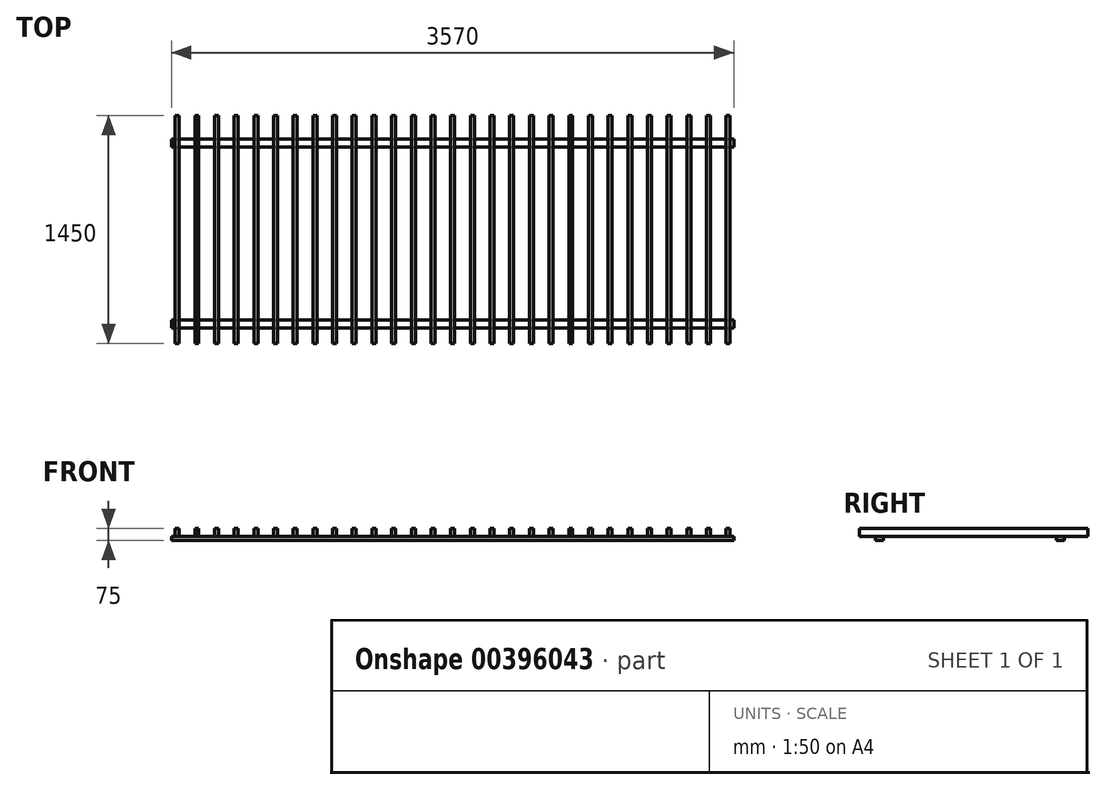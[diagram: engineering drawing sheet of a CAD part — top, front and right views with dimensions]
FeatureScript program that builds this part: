
annotation { "Feature Type Name" : "Feature", "Feature Type Description" : "" }
export const myFeature = defineFeature(function(context is Context, id is Id, definition is map)
    precondition{}
    {
        {
            var Q0;
            Q0=qCreatedBy(makeId("Top.planeOp"),FACE);
            var sketch = newSketch(context, id + "F0", { "sketchPlane" : qUnion([Q0])});
            skLineSegment(sketch, "E0.bottom", {"start": v(0, 0) * mm, "end": v(3570, 0) * mm, "construction": true});
            skLineSegment(sketch, "E0.top", {"start": v(0, 1500) * mm, "end": v(3570, 1500) * mm, "construction": true});
            skLineSegment(sketch, "E0.left", {"start": v(0, 0) * mm, "end": v(0, 1500) * mm, "construction": true});
            skLineSegment(sketch, "E0.right", {"start": v(3570, 0) * mm, "end": v(3570, 1500) * mm, "construction": true});
            skLineSegment(sketch, "E1", {"start": v(0, 750) * mm, "end": v(3570, 750) * mm, "construction": true});
            skLineSegment(sketch, "E2.bottom", {"start": v(22.5, 1500) * mm, "end": v(47.5, 1500) * mm});
            skLineSegment(sketch, "E2.top", {"start": v(22.5, 50) * mm, "end": v(47.5, 50) * mm});
            skLineSegment(sketch, "E2.left", {"start": v(22.5, 1500) * mm, "end": v(22.5, 50) * mm});
            skLineSegment(sketch, "E2.right", {"start": v(47.5, 1500) * mm, "end": v(47.5, 50) * mm});
            skLineSegment(sketch, "E3.1.0.0", {"start": v(147.5, 1500) * mm, "end": v(147.5, 50) * mm});
            skLineSegment(sketch, "E3.1.0.1", {"start": v(172.5, 1500) * mm, "end": v(172.5, 50) * mm});
            skLineSegment(sketch, "E3.1.0.2", {"start": v(147.5, 1500) * mm, "end": v(172.5, 1500) * mm});
            skLineSegment(sketch, "E3.1.0.3", {"start": v(147.5, 50) * mm, "end": v(172.5, 50) * mm});
            skLineSegment(sketch, "E3.2.0.0", {"start": v(272.5, 1500) * mm, "end": v(272.5, 50) * mm});
            skLineSegment(sketch, "E3.2.0.1", {"start": v(297.5, 1500) * mm, "end": v(297.5, 50) * mm});
            skLineSegment(sketch, "E3.2.0.2", {"start": v(272.5, 1500) * mm, "end": v(297.5, 1500) * mm});
            skLineSegment(sketch, "E3.2.0.3", {"start": v(272.5, 50) * mm, "end": v(297.5, 50) * mm});
            skLineSegment(sketch, "E3.3.0.0", {"start": v(397.5, 1500) * mm, "end": v(397.5, 50) * mm});
            skLineSegment(sketch, "E3.3.0.1", {"start": v(422.5, 1500) * mm, "end": v(422.5, 50) * mm});
            skLineSegment(sketch, "E3.3.0.2", {"start": v(397.5, 1500) * mm, "end": v(422.5, 1500) * mm});
            skLineSegment(sketch, "E3.3.0.3", {"start": v(397.5, 50) * mm, "end": v(422.5, 50) * mm});
            skLineSegment(sketch, "E3.4.0.0", {"start": v(522.5, 1500) * mm, "end": v(522.5, 50) * mm});
            skLineSegment(sketch, "E3.4.0.1", {"start": v(547.5, 1500) * mm, "end": v(547.5, 50) * mm});
            skLineSegment(sketch, "E3.4.0.2", {"start": v(522.5, 1500) * mm, "end": v(547.5, 1500) * mm});
            skLineSegment(sketch, "E3.4.0.3", {"start": v(522.5, 50) * mm, "end": v(547.5, 50) * mm});
            skLineSegment(sketch, "E3.5.0.0", {"start": v(647.5, 1500) * mm, "end": v(647.5, 50) * mm});
            skLineSegment(sketch, "E3.5.0.1", {"start": v(672.5, 1500) * mm, "end": v(672.5, 50) * mm});
            skLineSegment(sketch, "E3.5.0.2", {"start": v(647.5, 1500) * mm, "end": v(672.5, 1500) * mm});
            skLineSegment(sketch, "E3.5.0.3", {"start": v(647.5, 50) * mm, "end": v(672.5, 50) * mm});
            skLineSegment(sketch, "E3.6.0.0", {"start": v(772.5, 1500) * mm, "end": v(772.5, 50) * mm});
            skLineSegment(sketch, "E3.6.0.1", {"start": v(797.5, 1500) * mm, "end": v(797.5, 50) * mm});
            skLineSegment(sketch, "E3.6.0.2", {"start": v(772.5, 1500) * mm, "end": v(797.5, 1500) * mm});
            skLineSegment(sketch, "E3.6.0.3", {"start": v(772.5, 50) * mm, "end": v(797.5, 50) * mm});
            skLineSegment(sketch, "E3.7.0.0", {"start": v(897.5, 1500) * mm, "end": v(897.5, 50) * mm});
            skLineSegment(sketch, "E3.7.0.1", {"start": v(922.5, 1500) * mm, "end": v(922.5, 50) * mm});
            skLineSegment(sketch, "E3.7.0.2", {"start": v(897.5, 1500) * mm, "end": v(922.5, 1500) * mm});
            skLineSegment(sketch, "E3.7.0.3", {"start": v(897.5, 50) * mm, "end": v(922.5, 50) * mm});
            skLineSegment(sketch, "E3.8.0.0", {"start": v(1022.5, 1500) * mm, "end": v(1022.5, 50) * mm});
            skLineSegment(sketch, "E3.8.0.1", {"start": v(1047.5, 1500) * mm, "end": v(1047.5, 50) * mm});
            skLineSegment(sketch, "E3.8.0.2", {"start": v(1022.5, 1500) * mm, "end": v(1047.5, 1500) * mm});
            skLineSegment(sketch, "E3.8.0.3", {"start": v(1022.5, 50) * mm, "end": v(1047.5, 50) * mm});
            skLineSegment(sketch, "E3.9.0.0", {"start": v(1147.5, 1500) * mm, "end": v(1147.5, 50) * mm});
            skLineSegment(sketch, "E3.9.0.1", {"start": v(1172.5, 1500) * mm, "end": v(1172.5, 50) * mm});
            skLineSegment(sketch, "E3.9.0.2", {"start": v(1147.5, 1500) * mm, "end": v(1172.5, 1500) * mm});
            skLineSegment(sketch, "E3.9.0.3", {"start": v(1147.5, 50) * mm, "end": v(1172.5, 50) * mm});
            skLineSegment(sketch, "E3.10.0.0", {"start": v(1272.5, 1500) * mm, "end": v(1272.5, 50) * mm});
            skLineSegment(sketch, "E3.10.0.1", {"start": v(1297.5, 1500) * mm, "end": v(1297.5, 50) * mm});
            skLineSegment(sketch, "E3.10.0.2", {"start": v(1272.5, 1500) * mm, "end": v(1297.5, 1500) * mm});
            skLineSegment(sketch, "E3.10.0.3", {"start": v(1272.5, 50) * mm, "end": v(1297.5, 50) * mm});
            skLineSegment(sketch, "E3.11.0.0", {"start": v(1397.5, 1500) * mm, "end": v(1397.5, 50) * mm});
            skLineSegment(sketch, "E3.11.0.1", {"start": v(1422.5, 1500) * mm, "end": v(1422.5, 50) * mm});
            skLineSegment(sketch, "E3.11.0.2", {"start": v(1397.5, 1500) * mm, "end": v(1422.5, 1500) * mm});
            skLineSegment(sketch, "E3.11.0.3", {"start": v(1397.5, 50) * mm, "end": v(1422.5, 50) * mm});
            skLineSegment(sketch, "E3.12.0.0", {"start": v(1522.5, 1500) * mm, "end": v(1522.5, 50) * mm});
            skLineSegment(sketch, "E3.12.0.1", {"start": v(1547.5, 1500) * mm, "end": v(1547.5, 50) * mm});
            skLineSegment(sketch, "E3.12.0.2", {"start": v(1522.5, 1500) * mm, "end": v(1547.5, 1500) * mm});
            skLineSegment(sketch, "E3.12.0.3", {"start": v(1522.5, 50) * mm, "end": v(1547.5, 50) * mm});
            skLineSegment(sketch, "E3.13.0.0", {"start": v(1647.5, 1500) * mm, "end": v(1647.5, 50) * mm});
            skLineSegment(sketch, "E3.13.0.1", {"start": v(1672.5, 1500) * mm, "end": v(1672.5, 50) * mm});
            skLineSegment(sketch, "E3.13.0.2", {"start": v(1647.5, 1500) * mm, "end": v(1672.5, 1500) * mm});
            skLineSegment(sketch, "E3.13.0.3", {"start": v(1647.5, 50) * mm, "end": v(1672.5, 50) * mm});
            skLineSegment(sketch, "E3.14.0.0", {"start": v(1772.5, 1500) * mm, "end": v(1772.5, 50) * mm});
            skLineSegment(sketch, "E3.14.0.1", {"start": v(1797.5, 1500) * mm, "end": v(1797.5, 50) * mm});
            skLineSegment(sketch, "E3.14.0.2", {"start": v(1772.5, 1500) * mm, "end": v(1797.5, 1500) * mm});
            skLineSegment(sketch, "E3.14.0.3", {"start": v(1772.5, 50) * mm, "end": v(1797.5, 50) * mm});
            skLineSegment(sketch, "E3.direction1", {"start": v(22.5, 50) * mm, "end": v(147.5, 50) * mm, "construction": true});
            skLineSegment(sketch, "E4.0.15.0", {"start": v(1897.5, 1500) * mm, "end": v(1897.5, 50) * mm});
            skLineSegment(sketch, "E4.3.15.0", {"start": v(1922.5, 1500) * mm, "end": v(1922.5, 50) * mm});
            skLineSegment(sketch, "E4.6.15.0", {"start": v(1897.5, 1500) * mm, "end": v(1922.5, 1500) * mm});
            skLineSegment(sketch, "E4.9.15.0", {"start": v(1897.5, 50) * mm, "end": v(1922.5, 50) * mm});
            skLineSegment(sketch, "E5.0.16.0", {"start": v(2022.5, 1500) * mm, "end": v(2022.5, 50) * mm});
            skLineSegment(sketch, "E5.3.16.0", {"start": v(2047.5, 1500) * mm, "end": v(2047.5, 50) * mm});
            skLineSegment(sketch, "E5.6.16.0", {"start": v(2022.5, 1500) * mm, "end": v(2047.5, 1500) * mm});
            skLineSegment(sketch, "E5.9.16.0", {"start": v(2022.5, 50) * mm, "end": v(2047.5, 50) * mm});
            skLineSegment(sketch, "E5.0.17.0", {"start": v(2147.5, 1500) * mm, "end": v(2147.5, 50) * mm});
            skLineSegment(sketch, "E5.3.17.0", {"start": v(2172.5, 1500) * mm, "end": v(2172.5, 50) * mm});
            skLineSegment(sketch, "E5.6.17.0", {"start": v(2147.5, 1500) * mm, "end": v(2172.5, 1500) * mm});
            skLineSegment(sketch, "E5.9.17.0", {"start": v(2147.5, 50) * mm, "end": v(2172.5, 50) * mm});
            skLineSegment(sketch, "E5.0.18.0", {"start": v(2272.5, 1500) * mm, "end": v(2272.5, 50) * mm});
            skLineSegment(sketch, "E5.3.18.0", {"start": v(2297.5, 1500) * mm, "end": v(2297.5, 50) * mm});
            skLineSegment(sketch, "E5.6.18.0", {"start": v(2272.5, 1500) * mm, "end": v(2297.5, 1500) * mm});
            skLineSegment(sketch, "E5.9.18.0", {"start": v(2272.5, 50) * mm, "end": v(2297.5, 50) * mm});
            skLineSegment(sketch, "E5.0.19.0", {"start": v(2397.5, 1500) * mm, "end": v(2397.5, 50) * mm});
            skLineSegment(sketch, "E5.3.19.0", {"start": v(2422.5, 1500) * mm, "end": v(2422.5, 50) * mm});
            skLineSegment(sketch, "E5.6.19.0", {"start": v(2397.5, 1500) * mm, "end": v(2422.5, 1500) * mm});
            skLineSegment(sketch, "E5.9.19.0", {"start": v(2397.5, 50) * mm, "end": v(2422.5, 50) * mm});
            skLineSegment(sketch, "E5.0.20.0", {"start": v(2522.5, 1500) * mm, "end": v(2522.5, 50) * mm});
            skLineSegment(sketch, "E5.3.20.0", {"start": v(2547.5, 1500) * mm, "end": v(2547.5, 50) * mm});
            skLineSegment(sketch, "E5.6.20.0", {"start": v(2522.5, 1500) * mm, "end": v(2547.5, 1500) * mm});
            skLineSegment(sketch, "E5.9.20.0", {"start": v(2522.5, 50) * mm, "end": v(2547.5, 50) * mm});
            skLineSegment(sketch, "E5.0.21.0", {"start": v(2647.5, 1500) * mm, "end": v(2647.5, 50) * mm});
            skLineSegment(sketch, "E5.3.21.0", {"start": v(2672.5, 1500) * mm, "end": v(2672.5, 50) * mm});
            skLineSegment(sketch, "E5.6.21.0", {"start": v(2647.5, 1500) * mm, "end": v(2672.5, 1500) * mm});
            skLineSegment(sketch, "E5.9.21.0", {"start": v(2647.5, 50) * mm, "end": v(2672.5, 50) * mm});
            skLineSegment(sketch, "E5.0.22.0", {"start": v(2772.5, 1500) * mm, "end": v(2772.5, 50) * mm});
            skLineSegment(sketch, "E5.3.22.0", {"start": v(2797.5, 1500) * mm, "end": v(2797.5, 50) * mm});
            skLineSegment(sketch, "E5.6.22.0", {"start": v(2772.5, 1500) * mm, "end": v(2797.5, 1500) * mm});
            skLineSegment(sketch, "E5.9.22.0", {"start": v(2772.5, 50) * mm, "end": v(2797.5, 50) * mm});
            skLineSegment(sketch, "E6.0.23.0", {"start": v(2897.5, 1500) * mm, "end": v(2897.5, 50) * mm});
            skLineSegment(sketch, "E6.3.23.0", {"start": v(2922.5, 1500) * mm, "end": v(2922.5, 50) * mm});
            skLineSegment(sketch, "E6.6.23.0", {"start": v(2897.5, 1500) * mm, "end": v(2922.5, 1500) * mm});
            skLineSegment(sketch, "E6.9.23.0", {"start": v(2897.5, 50) * mm, "end": v(2922.5, 50) * mm});
            skLineSegment(sketch, "E6.0.24.0", {"start": v(3022.5, 1500) * mm, "end": v(3022.5, 50) * mm});
            skLineSegment(sketch, "E6.3.24.0", {"start": v(3047.5, 1500) * mm, "end": v(3047.5, 50) * mm});
            skLineSegment(sketch, "E6.6.24.0", {"start": v(3022.5, 1500) * mm, "end": v(3047.5, 1500) * mm});
            skLineSegment(sketch, "E6.9.24.0", {"start": v(3022.5, 50) * mm, "end": v(3047.5, 50) * mm});
            skLineSegment(sketch, "E6.0.25.0", {"start": v(3147.5, 1500) * mm, "end": v(3147.5, 50) * mm});
            skLineSegment(sketch, "E6.3.25.0", {"start": v(3172.5, 1500) * mm, "end": v(3172.5, 50) * mm});
            skLineSegment(sketch, "E6.6.25.0", {"start": v(3147.5, 1500) * mm, "end": v(3172.5, 1500) * mm});
            skLineSegment(sketch, "E6.9.25.0", {"start": v(3147.5, 50) * mm, "end": v(3172.5, 50) * mm});
            skLineSegment(sketch, "E6.0.26.0", {"start": v(3272.5, 1500) * mm, "end": v(3272.5, 50) * mm});
            skLineSegment(sketch, "E6.3.26.0", {"start": v(3297.5, 1500) * mm, "end": v(3297.5, 50) * mm});
            skLineSegment(sketch, "E6.6.26.0", {"start": v(3272.5, 1500) * mm, "end": v(3297.5, 1500) * mm});
            skLineSegment(sketch, "E6.9.26.0", {"start": v(3272.5, 50) * mm, "end": v(3297.5, 50) * mm});
            skLineSegment(sketch, "E6.0.27.0", {"start": v(3397.5, 1500) * mm, "end": v(3397.5, 50) * mm});
            skLineSegment(sketch, "E6.3.27.0", {"start": v(3422.5, 1500) * mm, "end": v(3422.5, 50) * mm});
            skLineSegment(sketch, "E6.6.27.0", {"start": v(3397.5, 1500) * mm, "end": v(3422.5, 1500) * mm});
            skLineSegment(sketch, "E6.9.27.0", {"start": v(3397.5, 50) * mm, "end": v(3422.5, 50) * mm});
            skLineSegment(sketch, "E7.0.28.0", {"start": v(3522.5, 1500) * mm, "end": v(3522.5, 50) * mm});
            skLineSegment(sketch, "E7.3.28.0", {"start": v(3547.5, 1500) * mm, "end": v(3547.5, 50) * mm});
            skLineSegment(sketch, "E7.6.28.0", {"start": v(3522.5, 1500) * mm, "end": v(3547.5, 1500) * mm});
            skLineSegment(sketch, "E7.9.28.0", {"start": v(3522.5, 50) * mm, "end": v(3547.5, 50) * mm});
            skSolve(sketch);
        }
        {
            var Q0;
            {var subQ5=sQuery(id+"F0.wireOp",EDGE,"E2.top");Q0=makeQuery(id+"F0.imprint","IMPRINT",FACE,{"disambiguationData":[TD([[makeQuery(id+"F0.imprint","IMPRINT",EDGE,{"derivedFrom":subQ5}),1.0]])]});}
            var Q1;
            {var subQ5=sQuery(id+"F0.wireOp",EDGE,"E3.1.0.3");Q1=makeQuery(id+"F0.imprint","IMPRINT",FACE,{"disambiguationData":[TD([[makeQuery(id+"F0.imprint","IMPRINT",EDGE,{"derivedFrom":subQ5}),1.0]])]});}
            var Q2;
            {var subQ5=sQuery(id+"F0.wireOp",EDGE,"E3.2.0.3");Q2=makeQuery(id+"F0.imprint","IMPRINT",FACE,{"disambiguationData":[TD([[makeQuery(id+"F0.imprint","IMPRINT",EDGE,{"derivedFrom":subQ5}),1.0]])]});}
            var Q3;
            {var subQ5=sQuery(id+"F0.wireOp",EDGE,"E3.3.0.3");Q3=makeQuery(id+"F0.imprint","IMPRINT",FACE,{"disambiguationData":[TD([[makeQuery(id+"F0.imprint","IMPRINT",EDGE,{"derivedFrom":subQ5}),1.0]])]});}
            var Q4;
            {var subQ5=sQuery(id+"F0.wireOp",EDGE,"E3.4.0.3");Q4=makeQuery(id+"F0.imprint","IMPRINT",FACE,{"disambiguationData":[TD([[makeQuery(id+"F0.imprint","IMPRINT",EDGE,{"derivedFrom":subQ5}),1.0]])]});}
            var Q5;
            {var subQ5=sQuery(id+"F0.wireOp",EDGE,"E3.5.0.3");Q5=makeQuery(id+"F0.imprint","IMPRINT",FACE,{"disambiguationData":[TD([[makeQuery(id+"F0.imprint","IMPRINT",EDGE,{"derivedFrom":subQ5}),1.0]])]});}
            var Q6;
            {var subQ5=sQuery(id+"F0.wireOp",EDGE,"E3.6.0.3");Q6=makeQuery(id+"F0.imprint","IMPRINT",FACE,{"disambiguationData":[TD([[makeQuery(id+"F0.imprint","IMPRINT",EDGE,{"derivedFrom":subQ5}),1.0]])]});}
            var Q7;
            {var subQ5=sQuery(id+"F0.wireOp",EDGE,"E3.7.0.3");Q7=makeQuery(id+"F0.imprint","IMPRINT",FACE,{"disambiguationData":[TD([[makeQuery(id+"F0.imprint","IMPRINT",EDGE,{"derivedFrom":subQ5}),1.0]])]});}
            var Q8;
            {var subQ5=sQuery(id+"F0.wireOp",EDGE,"E3.8.0.3");Q8=makeQuery(id+"F0.imprint","IMPRINT",FACE,{"disambiguationData":[TD([[makeQuery(id+"F0.imprint","IMPRINT",EDGE,{"derivedFrom":subQ5}),1.0]])]});}
            var Q9;
            {var subQ5=sQuery(id+"F0.wireOp",EDGE,"E3.9.0.3");Q9=makeQuery(id+"F0.imprint","IMPRINT",FACE,{"disambiguationData":[TD([[makeQuery(id+"F0.imprint","IMPRINT",EDGE,{"derivedFrom":subQ5}),1.0]])]});}
            var Q10;
            {var subQ5=sQuery(id+"F0.wireOp",EDGE,"E3.10.0.3");Q10=makeQuery(id+"F0.imprint","IMPRINT",FACE,{"disambiguationData":[TD([[makeQuery(id+"F0.imprint","IMPRINT",EDGE,{"derivedFrom":subQ5}),1.0]])]});}
            var Q11;
            {var subQ5=sQuery(id+"F0.wireOp",EDGE,"E3.11.0.3");Q11=makeQuery(id+"F0.imprint","IMPRINT",FACE,{"disambiguationData":[TD([[makeQuery(id+"F0.imprint","IMPRINT",EDGE,{"derivedFrom":subQ5}),1.0]])]});}
            var Q12;
            {var subQ5=sQuery(id+"F0.wireOp",EDGE,"E3.12.0.3");Q12=makeQuery(id+"F0.imprint","IMPRINT",FACE,{"disambiguationData":[TD([[makeQuery(id+"F0.imprint","IMPRINT",EDGE,{"derivedFrom":subQ5}),1.0]])]});}
            var Q13;
            {var subQ5=sQuery(id+"F0.wireOp",EDGE,"E3.13.0.3");Q13=makeQuery(id+"F0.imprint","IMPRINT",FACE,{"disambiguationData":[TD([[makeQuery(id+"F0.imprint","IMPRINT",EDGE,{"derivedFrom":subQ5}),1.0]])]});}
            var Q14;
            {var subQ5=sQuery(id+"F0.wireOp",EDGE,"E3.14.0.3");Q14=makeQuery(id+"F0.imprint","IMPRINT",FACE,{"disambiguationData":[TD([[makeQuery(id+"F0.imprint","IMPRINT",EDGE,{"derivedFrom":subQ5}),1.0]])]});}
            var Q15;
            {var subQ5=sQuery(id+"F0.wireOp",EDGE,"E4.9.15.0");Q15=makeQuery(id+"F0.imprint","IMPRINT",FACE,{"disambiguationData":[TD([[makeQuery(id+"F0.imprint","IMPRINT",EDGE,{"derivedFrom":subQ5}),1.0]])]});}
            var Q16;
            {var subQ5=sQuery(id+"F0.wireOp",EDGE,"E2.bottom");Q16=makeQuery(id+"F0.imprint","IMPRINT",FACE,{"disambiguationData":[TD([[makeQuery(id+"F0.imprint","IMPRINT",EDGE,{"derivedFrom":subQ5}),-1.0]])]});}
            var Q17;
            {var subQ5=sQuery(id+"F0.wireOp",EDGE,"E3.1.0.2");Q17=makeQuery(id+"F0.imprint","IMPRINT",FACE,{"disambiguationData":[TD([[makeQuery(id+"F0.imprint","IMPRINT",EDGE,{"derivedFrom":subQ5}),-1.0]])]});}
            var Q18;
            {var subQ5=sQuery(id+"F0.wireOp",EDGE,"E3.2.0.2");Q18=makeQuery(id+"F0.imprint","IMPRINT",FACE,{"disambiguationData":[TD([[makeQuery(id+"F0.imprint","IMPRINT",EDGE,{"derivedFrom":subQ5}),-1.0]])]});}
            var Q19;
            {var subQ5=sQuery(id+"F0.wireOp",EDGE,"E3.3.0.2");Q19=makeQuery(id+"F0.imprint","IMPRINT",FACE,{"disambiguationData":[TD([[makeQuery(id+"F0.imprint","IMPRINT",EDGE,{"derivedFrom":subQ5}),-1.0]])]});}
            var Q20;
            {var subQ5=sQuery(id+"F0.wireOp",EDGE,"E3.4.0.2");Q20=makeQuery(id+"F0.imprint","IMPRINT",FACE,{"disambiguationData":[TD([[makeQuery(id+"F0.imprint","IMPRINT",EDGE,{"derivedFrom":subQ5}),-1.0]])]});}
            var Q21;
            {var subQ5=sQuery(id+"F0.wireOp",EDGE,"E3.5.0.2");Q21=makeQuery(id+"F0.imprint","IMPRINT",FACE,{"disambiguationData":[TD([[makeQuery(id+"F0.imprint","IMPRINT",EDGE,{"derivedFrom":subQ5}),-1.0]])]});}
            var Q22;
            {var subQ5=sQuery(id+"F0.wireOp",EDGE,"E3.6.0.2");Q22=makeQuery(id+"F0.imprint","IMPRINT",FACE,{"disambiguationData":[TD([[makeQuery(id+"F0.imprint","IMPRINT",EDGE,{"derivedFrom":subQ5}),-1.0]])]});}
            var Q23;
            {var subQ5=sQuery(id+"F0.wireOp",EDGE,"E3.7.0.2");Q23=makeQuery(id+"F0.imprint","IMPRINT",FACE,{"disambiguationData":[TD([[makeQuery(id+"F0.imprint","IMPRINT",EDGE,{"derivedFrom":subQ5}),-1.0]])]});}
            var Q24;
            {var subQ5=sQuery(id+"F0.wireOp",EDGE,"E3.8.0.2");Q24=makeQuery(id+"F0.imprint","IMPRINT",FACE,{"disambiguationData":[TD([[makeQuery(id+"F0.imprint","IMPRINT",EDGE,{"derivedFrom":subQ5}),-1.0]])]});}
            var Q25;
            {var subQ5=sQuery(id+"F0.wireOp",EDGE,"E3.9.0.2");Q25=makeQuery(id+"F0.imprint","IMPRINT",FACE,{"disambiguationData":[TD([[makeQuery(id+"F0.imprint","IMPRINT",EDGE,{"derivedFrom":subQ5}),-1.0]])]});}
            var Q26;
            {var subQ5=sQuery(id+"F0.wireOp",EDGE,"E3.10.0.2");Q26=makeQuery(id+"F0.imprint","IMPRINT",FACE,{"disambiguationData":[TD([[makeQuery(id+"F0.imprint","IMPRINT",EDGE,{"derivedFrom":subQ5}),-1.0]])]});}
            var Q27;
            {var subQ5=sQuery(id+"F0.wireOp",EDGE,"E3.11.0.2");Q27=makeQuery(id+"F0.imprint","IMPRINT",FACE,{"disambiguationData":[TD([[makeQuery(id+"F0.imprint","IMPRINT",EDGE,{"derivedFrom":subQ5}),-1.0]])]});}
            var Q28;
            {var subQ5=sQuery(id+"F0.wireOp",EDGE,"E3.12.0.2");Q28=makeQuery(id+"F0.imprint","IMPRINT",FACE,{"disambiguationData":[TD([[makeQuery(id+"F0.imprint","IMPRINT",EDGE,{"derivedFrom":subQ5}),-1.0]])]});}
            var Q29;
            {var subQ5=sQuery(id+"F0.wireOp",EDGE,"E3.13.0.2");Q29=makeQuery(id+"F0.imprint","IMPRINT",FACE,{"disambiguationData":[TD([[makeQuery(id+"F0.imprint","IMPRINT",EDGE,{"derivedFrom":subQ5}),-1.0]])]});}
            var Q30;
            {var subQ5=sQuery(id+"F0.wireOp",EDGE,"E3.14.0.2");Q30=makeQuery(id+"F0.imprint","IMPRINT",FACE,{"disambiguationData":[TD([[makeQuery(id+"F0.imprint","IMPRINT",EDGE,{"derivedFrom":subQ5}),-1.0]])]});}
            var Q31;
            {var subQ5=sQuery(id+"F0.wireOp",EDGE,"E4.6.15.0");Q31=makeQuery(id+"F0.imprint","IMPRINT",FACE,{"disambiguationData":[TD([[makeQuery(id+"F0.imprint","IMPRINT",EDGE,{"derivedFrom":subQ5}),-1.0]])]});}
            var Q32;
            {var subQ0=sQuery(id+"F0.wireOp",EDGE,"E2.left");var subQ1=sQuery(id+"F0.wireOp",EDGE,"a2V2KlfY-Gady-qtY6-GD2h-aRWodLEw3NTq.top");var subQ2=makeQuery(id+"F0.imprint","INTERSECT",VERTEX,{"derivedFrom":[subQ1,subQ0]});Q32=makeQuery(id+"F0.imprint","IMPRINT",FACE,{"disambiguationData":[TD([[makeQuery(id+"F0.imprint","IMPRINT",EDGE,{"disambiguationData":[TD([[subQ2,-1.0]])],"derivedFrom":subQ1}),1.0]])]});}
            var Q33;
            {var subQ0=sQuery(id+"F0.wireOp",EDGE,"E4.3.15.0");var subQ1=sQuery(id+"F0.wireOp",EDGE,"a2V2KlfY-Gady-qtY6-GD2h-aRWodLEw3NTq.top");var subQ2=makeQuery(id+"F0.imprint","INTERSECT",VERTEX,{"derivedFrom":[subQ1,subQ0]});Q33=makeQuery(id+"F0.imprint","IMPRINT",FACE,{"disambiguationData":[TD([[makeQuery(id+"F0.imprint","IMPRINT",EDGE,{"disambiguationData":[TD([[subQ2,1.0]])],"derivedFrom":subQ1}),1.0]])]});}
            var Q34;
            {var subQ0=sQuery(id+"F0.wireOp",EDGE,"E2.left");var subQ1=sQuery(id+"F0.wireOp",EDGE,"a2V2KlfY-Gady-qtY6-GD2h-aRWodLEw3NTq.bottom");var subQ2=makeQuery(id+"F0.imprint","INTERSECT",VERTEX,{"derivedFrom":[subQ1,subQ0]});Q34=makeQuery(id+"F0.imprint","IMPRINT",FACE,{"disambiguationData":[TD([[makeQuery(id+"F0.imprint","IMPRINT",EDGE,{"disambiguationData":[TD([[subQ2,-1.0]])],"derivedFrom":subQ1}),1.0]])]});}
            var Q35;
            {var subQ0=sQuery(id+"F0.wireOp",EDGE,"E3.1.0.0");var subQ1=sQuery(id+"F0.wireOp",EDGE,"a2V2KlfY-Gady-qtY6-GD2h-aRWodLEw3NTq.bottom");var subQ2=makeQuery(id+"F0.imprint","INTERSECT",VERTEX,{"derivedFrom":[subQ1,subQ0]});Q35=makeQuery(id+"F0.imprint","IMPRINT",FACE,{"disambiguationData":[TD([[makeQuery(id+"F0.imprint","IMPRINT",EDGE,{"disambiguationData":[TD([[subQ2,-1.0]])],"derivedFrom":subQ1}),1.0]])]});}
            var Q36;
            {var subQ0=sQuery(id+"F0.wireOp",EDGE,"E3.2.0.0");var subQ1=sQuery(id+"F0.wireOp",EDGE,"a2V2KlfY-Gady-qtY6-GD2h-aRWodLEw3NTq.bottom");var subQ2=makeQuery(id+"F0.imprint","INTERSECT",VERTEX,{"derivedFrom":[subQ1,subQ0]});Q36=makeQuery(id+"F0.imprint","IMPRINT",FACE,{"disambiguationData":[TD([[makeQuery(id+"F0.imprint","IMPRINT",EDGE,{"disambiguationData":[TD([[subQ2,-1.0]])],"derivedFrom":subQ1}),1.0]])]});}
            var Q37;
            {var subQ0=sQuery(id+"F0.wireOp",EDGE,"E3.3.0.0");var subQ1=sQuery(id+"F0.wireOp",EDGE,"a2V2KlfY-Gady-qtY6-GD2h-aRWodLEw3NTq.bottom");var subQ2=makeQuery(id+"F0.imprint","INTERSECT",VERTEX,{"derivedFrom":[subQ1,subQ0]});Q37=makeQuery(id+"F0.imprint","IMPRINT",FACE,{"disambiguationData":[TD([[makeQuery(id+"F0.imprint","IMPRINT",EDGE,{"disambiguationData":[TD([[subQ2,-1.0]])],"derivedFrom":subQ1}),1.0]])]});}
            var Q38;
            {var subQ0=sQuery(id+"F0.wireOp",EDGE,"E3.4.0.0");var subQ1=sQuery(id+"F0.wireOp",EDGE,"a2V2KlfY-Gady-qtY6-GD2h-aRWodLEw3NTq.bottom");var subQ2=makeQuery(id+"F0.imprint","INTERSECT",VERTEX,{"derivedFrom":[subQ1,subQ0]});Q38=makeQuery(id+"F0.imprint","IMPRINT",FACE,{"disambiguationData":[TD([[makeQuery(id+"F0.imprint","IMPRINT",EDGE,{"disambiguationData":[TD([[subQ2,-1.0]])],"derivedFrom":subQ1}),1.0]])]});}
            var Q39;
            {var subQ0=sQuery(id+"F0.wireOp",EDGE,"E3.5.0.0");var subQ1=sQuery(id+"F0.wireOp",EDGE,"a2V2KlfY-Gady-qtY6-GD2h-aRWodLEw3NTq.bottom");var subQ2=makeQuery(id+"F0.imprint","INTERSECT",VERTEX,{"derivedFrom":[subQ1,subQ0]});Q39=makeQuery(id+"F0.imprint","IMPRINT",FACE,{"disambiguationData":[TD([[makeQuery(id+"F0.imprint","IMPRINT",EDGE,{"disambiguationData":[TD([[subQ2,-1.0]])],"derivedFrom":subQ1}),1.0]])]});}
            var Q40;
            {var subQ0=sQuery(id+"F0.wireOp",EDGE,"E3.6.0.0");var subQ1=sQuery(id+"F0.wireOp",EDGE,"a2V2KlfY-Gady-qtY6-GD2h-aRWodLEw3NTq.bottom");var subQ2=makeQuery(id+"F0.imprint","INTERSECT",VERTEX,{"derivedFrom":[subQ1,subQ0]});Q40=makeQuery(id+"F0.imprint","IMPRINT",FACE,{"disambiguationData":[TD([[makeQuery(id+"F0.imprint","IMPRINT",EDGE,{"disambiguationData":[TD([[subQ2,-1.0]])],"derivedFrom":subQ1}),1.0]])]});}
            var Q41;
            {var subQ0=sQuery(id+"F0.wireOp",EDGE,"E3.7.0.0");var subQ1=sQuery(id+"F0.wireOp",EDGE,"a2V2KlfY-Gady-qtY6-GD2h-aRWodLEw3NTq.bottom");var subQ2=makeQuery(id+"F0.imprint","INTERSECT",VERTEX,{"derivedFrom":[subQ1,subQ0]});Q41=makeQuery(id+"F0.imprint","IMPRINT",FACE,{"disambiguationData":[TD([[makeQuery(id+"F0.imprint","IMPRINT",EDGE,{"disambiguationData":[TD([[subQ2,-1.0]])],"derivedFrom":subQ1}),1.0]])]});}
            var Q42;
            {var subQ0=sQuery(id+"F0.wireOp",EDGE,"E3.8.0.0");var subQ1=sQuery(id+"F0.wireOp",EDGE,"a2V2KlfY-Gady-qtY6-GD2h-aRWodLEw3NTq.bottom");var subQ2=makeQuery(id+"F0.imprint","INTERSECT",VERTEX,{"derivedFrom":[subQ1,subQ0]});Q42=makeQuery(id+"F0.imprint","IMPRINT",FACE,{"disambiguationData":[TD([[makeQuery(id+"F0.imprint","IMPRINT",EDGE,{"disambiguationData":[TD([[subQ2,-1.0]])],"derivedFrom":subQ1}),1.0]])]});}
            var Q43;
            {var subQ0=sQuery(id+"F0.wireOp",EDGE,"E3.9.0.0");var subQ1=sQuery(id+"F0.wireOp",EDGE,"a2V2KlfY-Gady-qtY6-GD2h-aRWodLEw3NTq.bottom");var subQ2=makeQuery(id+"F0.imprint","INTERSECT",VERTEX,{"derivedFrom":[subQ1,subQ0]});Q43=makeQuery(id+"F0.imprint","IMPRINT",FACE,{"disambiguationData":[TD([[makeQuery(id+"F0.imprint","IMPRINT",EDGE,{"disambiguationData":[TD([[subQ2,-1.0]])],"derivedFrom":subQ1}),1.0]])]});}
            var Q44;
            {var subQ0=sQuery(id+"F0.wireOp",EDGE,"E3.10.0.0");var subQ1=sQuery(id+"F0.wireOp",EDGE,"a2V2KlfY-Gady-qtY6-GD2h-aRWodLEw3NTq.bottom");var subQ2=makeQuery(id+"F0.imprint","INTERSECT",VERTEX,{"derivedFrom":[subQ1,subQ0]});Q44=makeQuery(id+"F0.imprint","IMPRINT",FACE,{"disambiguationData":[TD([[makeQuery(id+"F0.imprint","IMPRINT",EDGE,{"disambiguationData":[TD([[subQ2,-1.0]])],"derivedFrom":subQ1}),1.0]])]});}
            var Q45;
            {var subQ0=sQuery(id+"F0.wireOp",EDGE,"E3.11.0.0");var subQ1=sQuery(id+"F0.wireOp",EDGE,"a2V2KlfY-Gady-qtY6-GD2h-aRWodLEw3NTq.bottom");var subQ2=makeQuery(id+"F0.imprint","INTERSECT",VERTEX,{"derivedFrom":[subQ1,subQ0]});Q45=makeQuery(id+"F0.imprint","IMPRINT",FACE,{"disambiguationData":[TD([[makeQuery(id+"F0.imprint","IMPRINT",EDGE,{"disambiguationData":[TD([[subQ2,-1.0]])],"derivedFrom":subQ1}),1.0]])]});}
            var Q46;
            {var subQ0=sQuery(id+"F0.wireOp",EDGE,"E3.12.0.0");var subQ1=sQuery(id+"F0.wireOp",EDGE,"a2V2KlfY-Gady-qtY6-GD2h-aRWodLEw3NTq.bottom");var subQ2=makeQuery(id+"F0.imprint","INTERSECT",VERTEX,{"derivedFrom":[subQ1,subQ0]});Q46=makeQuery(id+"F0.imprint","IMPRINT",FACE,{"disambiguationData":[TD([[makeQuery(id+"F0.imprint","IMPRINT",EDGE,{"disambiguationData":[TD([[subQ2,-1.0]])],"derivedFrom":subQ1}),1.0]])]});}
            var Q47;
            {var subQ0=sQuery(id+"F0.wireOp",EDGE,"E3.13.0.0");var subQ1=sQuery(id+"F0.wireOp",EDGE,"a2V2KlfY-Gady-qtY6-GD2h-aRWodLEw3NTq.bottom");var subQ2=makeQuery(id+"F0.imprint","INTERSECT",VERTEX,{"derivedFrom":[subQ1,subQ0]});Q47=makeQuery(id+"F0.imprint","IMPRINT",FACE,{"disambiguationData":[TD([[makeQuery(id+"F0.imprint","IMPRINT",EDGE,{"disambiguationData":[TD([[subQ2,-1.0]])],"derivedFrom":subQ1}),1.0]])]});}
            var Q48;
            {var subQ0=sQuery(id+"F0.wireOp",EDGE,"E3.14.0.0");var subQ1=sQuery(id+"F0.wireOp",EDGE,"a2V2KlfY-Gady-qtY6-GD2h-aRWodLEw3NTq.bottom");var subQ2=makeQuery(id+"F0.imprint","INTERSECT",VERTEX,{"derivedFrom":[subQ1,subQ0]});Q48=makeQuery(id+"F0.imprint","IMPRINT",FACE,{"disambiguationData":[TD([[makeQuery(id+"F0.imprint","IMPRINT",EDGE,{"disambiguationData":[TD([[subQ2,-1.0]])],"derivedFrom":subQ1}),1.0]])]});}
            var Q49;
            {var subQ0=sQuery(id+"F0.wireOp",EDGE,"E4.0.15.0");var subQ1=sQuery(id+"F0.wireOp",EDGE,"a2V2KlfY-Gady-qtY6-GD2h-aRWodLEw3NTq.bottom");var subQ2=makeQuery(id+"F0.imprint","INTERSECT",VERTEX,{"derivedFrom":[subQ1,subQ0]});Q49=makeQuery(id+"F0.imprint","IMPRINT",FACE,{"disambiguationData":[TD([[makeQuery(id+"F0.imprint","IMPRINT",EDGE,{"disambiguationData":[TD([[subQ2,-1.0]])],"derivedFrom":subQ1}),1.0]])]});}
            var Q50;
            {var subQ0=sQuery(id+"F0.wireOp",EDGE,"E2.left");var subQ1=sQuery(id+"F0.wireOp",EDGE,"8b8792b9-98fa-49d1-87db-a45c0125a6752.MirrorCS");var subQ2=makeQuery(id+"F0.imprint","INTERSECT",VERTEX,{"derivedFrom":[subQ1,subQ0]});Q50=makeQuery(id+"F0.imprint","IMPRINT",FACE,{"disambiguationData":[TD([[makeQuery(id+"F0.imprint","IMPRINT",EDGE,{"disambiguationData":[TD([[subQ2,-1.0]])],"derivedFrom":subQ1}),-1.0]])]});}
            var Q51;
            {var subQ0=sQuery(id+"F0.wireOp",EDGE,"E3.1.0.0");var subQ1=sQuery(id+"F0.wireOp",EDGE,"8b8792b9-98fa-49d1-87db-a45c0125a6752.MirrorCS");var subQ2=makeQuery(id+"F0.imprint","INTERSECT",VERTEX,{"derivedFrom":[subQ1,subQ0]});Q51=makeQuery(id+"F0.imprint","IMPRINT",FACE,{"disambiguationData":[TD([[makeQuery(id+"F0.imprint","IMPRINT",EDGE,{"disambiguationData":[TD([[subQ2,-1.0]])],"derivedFrom":subQ1}),-1.0]])]});}
            var Q52;
            {var subQ0=sQuery(id+"F0.wireOp",EDGE,"E3.2.0.0");var subQ1=sQuery(id+"F0.wireOp",EDGE,"8b8792b9-98fa-49d1-87db-a45c0125a6752.MirrorCS");var subQ2=makeQuery(id+"F0.imprint","INTERSECT",VERTEX,{"derivedFrom":[subQ1,subQ0]});Q52=makeQuery(id+"F0.imprint","IMPRINT",FACE,{"disambiguationData":[TD([[makeQuery(id+"F0.imprint","IMPRINT",EDGE,{"disambiguationData":[TD([[subQ2,-1.0]])],"derivedFrom":subQ1}),-1.0]])]});}
            var Q53;
            {var subQ0=sQuery(id+"F0.wireOp",EDGE,"E3.3.0.0");var subQ1=sQuery(id+"F0.wireOp",EDGE,"8b8792b9-98fa-49d1-87db-a45c0125a6752.MirrorCS");var subQ2=makeQuery(id+"F0.imprint","INTERSECT",VERTEX,{"derivedFrom":[subQ1,subQ0]});Q53=makeQuery(id+"F0.imprint","IMPRINT",FACE,{"disambiguationData":[TD([[makeQuery(id+"F0.imprint","IMPRINT",EDGE,{"disambiguationData":[TD([[subQ2,-1.0]])],"derivedFrom":subQ1}),-1.0]])]});}
            var Q54;
            {var subQ0=sQuery(id+"F0.wireOp",EDGE,"E3.4.0.0");var subQ1=sQuery(id+"F0.wireOp",EDGE,"8b8792b9-98fa-49d1-87db-a45c0125a6752.MirrorCS");var subQ2=makeQuery(id+"F0.imprint","INTERSECT",VERTEX,{"derivedFrom":[subQ1,subQ0]});Q54=makeQuery(id+"F0.imprint","IMPRINT",FACE,{"disambiguationData":[TD([[makeQuery(id+"F0.imprint","IMPRINT",EDGE,{"disambiguationData":[TD([[subQ2,-1.0]])],"derivedFrom":subQ1}),-1.0]])]});}
            var Q55;
            {var subQ0=sQuery(id+"F0.wireOp",EDGE,"E3.5.0.0");var subQ1=sQuery(id+"F0.wireOp",EDGE,"8b8792b9-98fa-49d1-87db-a45c0125a6752.MirrorCS");var subQ2=makeQuery(id+"F0.imprint","INTERSECT",VERTEX,{"derivedFrom":[subQ1,subQ0]});Q55=makeQuery(id+"F0.imprint","IMPRINT",FACE,{"disambiguationData":[TD([[makeQuery(id+"F0.imprint","IMPRINT",EDGE,{"disambiguationData":[TD([[subQ2,-1.0]])],"derivedFrom":subQ1}),-1.0]])]});}
            var Q56;
            {var subQ0=sQuery(id+"F0.wireOp",EDGE,"E3.6.0.0");var subQ1=sQuery(id+"F0.wireOp",EDGE,"8b8792b9-98fa-49d1-87db-a45c0125a6752.MirrorCS");var subQ2=makeQuery(id+"F0.imprint","INTERSECT",VERTEX,{"derivedFrom":[subQ1,subQ0]});Q56=makeQuery(id+"F0.imprint","IMPRINT",FACE,{"disambiguationData":[TD([[makeQuery(id+"F0.imprint","IMPRINT",EDGE,{"disambiguationData":[TD([[subQ2,-1.0]])],"derivedFrom":subQ1}),-1.0]])]});}
            var Q57;
            {var subQ0=sQuery(id+"F0.wireOp",EDGE,"E3.7.0.0");var subQ1=sQuery(id+"F0.wireOp",EDGE,"8b8792b9-98fa-49d1-87db-a45c0125a6752.MirrorCS");var subQ2=makeQuery(id+"F0.imprint","INTERSECT",VERTEX,{"derivedFrom":[subQ1,subQ0]});Q57=makeQuery(id+"F0.imprint","IMPRINT",FACE,{"disambiguationData":[TD([[makeQuery(id+"F0.imprint","IMPRINT",EDGE,{"disambiguationData":[TD([[subQ2,-1.0]])],"derivedFrom":subQ1}),-1.0]])]});}
            var Q58;
            {var subQ0=sQuery(id+"F0.wireOp",EDGE,"E3.8.0.0");var subQ1=sQuery(id+"F0.wireOp",EDGE,"8b8792b9-98fa-49d1-87db-a45c0125a6752.MirrorCS");var subQ2=makeQuery(id+"F0.imprint","INTERSECT",VERTEX,{"derivedFrom":[subQ1,subQ0]});Q58=makeQuery(id+"F0.imprint","IMPRINT",FACE,{"disambiguationData":[TD([[makeQuery(id+"F0.imprint","IMPRINT",EDGE,{"disambiguationData":[TD([[subQ2,-1.0]])],"derivedFrom":subQ1}),-1.0]])]});}
            var Q59;
            {var subQ0=sQuery(id+"F0.wireOp",EDGE,"E3.9.0.0");var subQ1=sQuery(id+"F0.wireOp",EDGE,"8b8792b9-98fa-49d1-87db-a45c0125a6752.MirrorCS");var subQ2=makeQuery(id+"F0.imprint","INTERSECT",VERTEX,{"derivedFrom":[subQ1,subQ0]});Q59=makeQuery(id+"F0.imprint","IMPRINT",FACE,{"disambiguationData":[TD([[makeQuery(id+"F0.imprint","IMPRINT",EDGE,{"disambiguationData":[TD([[subQ2,-1.0]])],"derivedFrom":subQ1}),-1.0]])]});}
            var Q60;
            {var subQ0=sQuery(id+"F0.wireOp",EDGE,"E3.10.0.0");var subQ1=sQuery(id+"F0.wireOp",EDGE,"8b8792b9-98fa-49d1-87db-a45c0125a6752.MirrorCS");var subQ2=makeQuery(id+"F0.imprint","INTERSECT",VERTEX,{"derivedFrom":[subQ1,subQ0]});Q60=makeQuery(id+"F0.imprint","IMPRINT",FACE,{"disambiguationData":[TD([[makeQuery(id+"F0.imprint","IMPRINT",EDGE,{"disambiguationData":[TD([[subQ2,-1.0]])],"derivedFrom":subQ1}),-1.0]])]});}
            var Q61;
            {var subQ0=sQuery(id+"F0.wireOp",EDGE,"E3.11.0.0");var subQ1=sQuery(id+"F0.wireOp",EDGE,"8b8792b9-98fa-49d1-87db-a45c0125a6752.MirrorCS");var subQ2=makeQuery(id+"F0.imprint","INTERSECT",VERTEX,{"derivedFrom":[subQ1,subQ0]});Q61=makeQuery(id+"F0.imprint","IMPRINT",FACE,{"disambiguationData":[TD([[makeQuery(id+"F0.imprint","IMPRINT",EDGE,{"disambiguationData":[TD([[subQ2,-1.0]])],"derivedFrom":subQ1}),-1.0]])]});}
            var Q62;
            {var subQ0=sQuery(id+"F0.wireOp",EDGE,"E3.12.0.0");var subQ1=sQuery(id+"F0.wireOp",EDGE,"8b8792b9-98fa-49d1-87db-a45c0125a6752.MirrorCS");var subQ2=makeQuery(id+"F0.imprint","INTERSECT",VERTEX,{"derivedFrom":[subQ1,subQ0]});Q62=makeQuery(id+"F0.imprint","IMPRINT",FACE,{"disambiguationData":[TD([[makeQuery(id+"F0.imprint","IMPRINT",EDGE,{"disambiguationData":[TD([[subQ2,-1.0]])],"derivedFrom":subQ1}),-1.0]])]});}
            var Q63;
            {var subQ0=sQuery(id+"F0.wireOp",EDGE,"E3.13.0.0");var subQ1=sQuery(id+"F0.wireOp",EDGE,"8b8792b9-98fa-49d1-87db-a45c0125a6752.MirrorCS");var subQ2=makeQuery(id+"F0.imprint","INTERSECT",VERTEX,{"derivedFrom":[subQ1,subQ0]});Q63=makeQuery(id+"F0.imprint","IMPRINT",FACE,{"disambiguationData":[TD([[makeQuery(id+"F0.imprint","IMPRINT",EDGE,{"disambiguationData":[TD([[subQ2,-1.0]])],"derivedFrom":subQ1}),-1.0]])]});}
            var Q64;
            {var subQ0=sQuery(id+"F0.wireOp",EDGE,"E3.14.0.0");var subQ1=sQuery(id+"F0.wireOp",EDGE,"8b8792b9-98fa-49d1-87db-a45c0125a6752.MirrorCS");var subQ2=makeQuery(id+"F0.imprint","INTERSECT",VERTEX,{"derivedFrom":[subQ1,subQ0]});Q64=makeQuery(id+"F0.imprint","IMPRINT",FACE,{"disambiguationData":[TD([[makeQuery(id+"F0.imprint","IMPRINT",EDGE,{"disambiguationData":[TD([[subQ2,-1.0]])],"derivedFrom":subQ1}),-1.0]])]});}
            var Q65;
            {var subQ0=sQuery(id+"F0.wireOp",EDGE,"E4.0.15.0");var subQ1=sQuery(id+"F0.wireOp",EDGE,"8b8792b9-98fa-49d1-87db-a45c0125a6752.MirrorCS");var subQ2=makeQuery(id+"F0.imprint","INTERSECT",VERTEX,{"derivedFrom":[subQ1,subQ0]});Q65=makeQuery(id+"F0.imprint","IMPRINT",FACE,{"disambiguationData":[TD([[makeQuery(id+"F0.imprint","IMPRINT",EDGE,{"disambiguationData":[TD([[subQ2,-1.0]])],"derivedFrom":subQ1}),-1.0]])]});}
            var Q66;
            {var subQ0=sQuery(id+"F0.wireOp",EDGE,"E3.1.0.0");var subQ1=sQuery(id+"F0.wireOp",EDGE,"a2V2KlfY-Gady-qtY6-GD2h-aRWodLEw3NTq.top");var subQ2=makeQuery(id+"F0.imprint","INTERSECT",VERTEX,{"derivedFrom":[subQ1,subQ0]});Q66=makeQuery(id+"F0.imprint","IMPRINT",FACE,{"disambiguationData":[TD([[makeQuery(id+"F0.imprint","IMPRINT",EDGE,{"disambiguationData":[TD([[subQ2,-1.0]])],"derivedFrom":subQ1}),1.0]])]});}
            var Q67;
            {var subQ0=sQuery(id+"F0.wireOp",EDGE,"E3.2.0.0");var subQ1=sQuery(id+"F0.wireOp",EDGE,"a2V2KlfY-Gady-qtY6-GD2h-aRWodLEw3NTq.top");var subQ2=makeQuery(id+"F0.imprint","INTERSECT",VERTEX,{"derivedFrom":[subQ1,subQ0]});Q67=makeQuery(id+"F0.imprint","IMPRINT",FACE,{"disambiguationData":[TD([[makeQuery(id+"F0.imprint","IMPRINT",EDGE,{"disambiguationData":[TD([[subQ2,-1.0]])],"derivedFrom":subQ1}),1.0]])]});}
            var Q68;
            {var subQ0=sQuery(id+"F0.wireOp",EDGE,"E3.3.0.0");var subQ1=sQuery(id+"F0.wireOp",EDGE,"a2V2KlfY-Gady-qtY6-GD2h-aRWodLEw3NTq.top");var subQ2=makeQuery(id+"F0.imprint","INTERSECT",VERTEX,{"derivedFrom":[subQ1,subQ0]});Q68=makeQuery(id+"F0.imprint","IMPRINT",FACE,{"disambiguationData":[TD([[makeQuery(id+"F0.imprint","IMPRINT",EDGE,{"disambiguationData":[TD([[subQ2,-1.0]])],"derivedFrom":subQ1}),1.0]])]});}
            var Q69;
            {var subQ0=sQuery(id+"F0.wireOp",EDGE,"E3.4.0.0");var subQ1=sQuery(id+"F0.wireOp",EDGE,"a2V2KlfY-Gady-qtY6-GD2h-aRWodLEw3NTq.top");var subQ2=makeQuery(id+"F0.imprint","INTERSECT",VERTEX,{"derivedFrom":[subQ1,subQ0]});Q69=makeQuery(id+"F0.imprint","IMPRINT",FACE,{"disambiguationData":[TD([[makeQuery(id+"F0.imprint","IMPRINT",EDGE,{"disambiguationData":[TD([[subQ2,-1.0]])],"derivedFrom":subQ1}),1.0]])]});}
            var Q70;
            {var subQ0=sQuery(id+"F0.wireOp",EDGE,"E3.5.0.0");var subQ1=sQuery(id+"F0.wireOp",EDGE,"a2V2KlfY-Gady-qtY6-GD2h-aRWodLEw3NTq.top");var subQ2=makeQuery(id+"F0.imprint","INTERSECT",VERTEX,{"derivedFrom":[subQ1,subQ0]});Q70=makeQuery(id+"F0.imprint","IMPRINT",FACE,{"disambiguationData":[TD([[makeQuery(id+"F0.imprint","IMPRINT",EDGE,{"disambiguationData":[TD([[subQ2,-1.0]])],"derivedFrom":subQ1}),1.0]])]});}
            var Q71;
            {var subQ0=sQuery(id+"F0.wireOp",EDGE,"E3.6.0.0");var subQ1=sQuery(id+"F0.wireOp",EDGE,"a2V2KlfY-Gady-qtY6-GD2h-aRWodLEw3NTq.top");var subQ2=makeQuery(id+"F0.imprint","INTERSECT",VERTEX,{"derivedFrom":[subQ1,subQ0]});Q71=makeQuery(id+"F0.imprint","IMPRINT",FACE,{"disambiguationData":[TD([[makeQuery(id+"F0.imprint","IMPRINT",EDGE,{"disambiguationData":[TD([[subQ2,-1.0]])],"derivedFrom":subQ1}),1.0]])]});}
            var Q72;
            {var subQ0=sQuery(id+"F0.wireOp",EDGE,"E3.7.0.0");var subQ1=sQuery(id+"F0.wireOp",EDGE,"a2V2KlfY-Gady-qtY6-GD2h-aRWodLEw3NTq.top");var subQ2=makeQuery(id+"F0.imprint","INTERSECT",VERTEX,{"derivedFrom":[subQ1,subQ0]});Q72=makeQuery(id+"F0.imprint","IMPRINT",FACE,{"disambiguationData":[TD([[makeQuery(id+"F0.imprint","IMPRINT",EDGE,{"disambiguationData":[TD([[subQ2,-1.0]])],"derivedFrom":subQ1}),1.0]])]});}
            var Q73;
            {var subQ0=sQuery(id+"F0.wireOp",EDGE,"E3.8.0.0");var subQ1=sQuery(id+"F0.wireOp",EDGE,"a2V2KlfY-Gady-qtY6-GD2h-aRWodLEw3NTq.top");var subQ2=makeQuery(id+"F0.imprint","INTERSECT",VERTEX,{"derivedFrom":[subQ1,subQ0]});Q73=makeQuery(id+"F0.imprint","IMPRINT",FACE,{"disambiguationData":[TD([[makeQuery(id+"F0.imprint","IMPRINT",EDGE,{"disambiguationData":[TD([[subQ2,-1.0]])],"derivedFrom":subQ1}),1.0]])]});}
            var Q74;
            {var subQ0=sQuery(id+"F0.wireOp",EDGE,"E3.9.0.0");var subQ1=sQuery(id+"F0.wireOp",EDGE,"a2V2KlfY-Gady-qtY6-GD2h-aRWodLEw3NTq.top");var subQ2=makeQuery(id+"F0.imprint","INTERSECT",VERTEX,{"derivedFrom":[subQ1,subQ0]});Q74=makeQuery(id+"F0.imprint","IMPRINT",FACE,{"disambiguationData":[TD([[makeQuery(id+"F0.imprint","IMPRINT",EDGE,{"disambiguationData":[TD([[subQ2,-1.0]])],"derivedFrom":subQ1}),1.0]])]});}
            var Q75;
            {var subQ0=sQuery(id+"F0.wireOp",EDGE,"E3.10.0.0");var subQ1=sQuery(id+"F0.wireOp",EDGE,"a2V2KlfY-Gady-qtY6-GD2h-aRWodLEw3NTq.top");var subQ2=makeQuery(id+"F0.imprint","INTERSECT",VERTEX,{"derivedFrom":[subQ1,subQ0]});Q75=makeQuery(id+"F0.imprint","IMPRINT",FACE,{"disambiguationData":[TD([[makeQuery(id+"F0.imprint","IMPRINT",EDGE,{"disambiguationData":[TD([[subQ2,-1.0]])],"derivedFrom":subQ1}),1.0]])]});}
            var Q76;
            {var subQ0=sQuery(id+"F0.wireOp",EDGE,"E3.11.0.0");var subQ1=sQuery(id+"F0.wireOp",EDGE,"a2V2KlfY-Gady-qtY6-GD2h-aRWodLEw3NTq.top");var subQ2=makeQuery(id+"F0.imprint","INTERSECT",VERTEX,{"derivedFrom":[subQ1,subQ0]});Q76=makeQuery(id+"F0.imprint","IMPRINT",FACE,{"disambiguationData":[TD([[makeQuery(id+"F0.imprint","IMPRINT",EDGE,{"disambiguationData":[TD([[subQ2,-1.0]])],"derivedFrom":subQ1}),1.0]])]});}
            var Q77;
            {var subQ0=sQuery(id+"F0.wireOp",EDGE,"E3.12.0.0");var subQ1=sQuery(id+"F0.wireOp",EDGE,"a2V2KlfY-Gady-qtY6-GD2h-aRWodLEw3NTq.top");var subQ2=makeQuery(id+"F0.imprint","INTERSECT",VERTEX,{"derivedFrom":[subQ1,subQ0]});Q77=makeQuery(id+"F0.imprint","IMPRINT",FACE,{"disambiguationData":[TD([[makeQuery(id+"F0.imprint","IMPRINT",EDGE,{"disambiguationData":[TD([[subQ2,-1.0]])],"derivedFrom":subQ1}),1.0]])]});}
            var Q78;
            {var subQ0=sQuery(id+"F0.wireOp",EDGE,"E3.13.0.0");var subQ1=sQuery(id+"F0.wireOp",EDGE,"a2V2KlfY-Gady-qtY6-GD2h-aRWodLEw3NTq.top");var subQ2=makeQuery(id+"F0.imprint","INTERSECT",VERTEX,{"derivedFrom":[subQ1,subQ0]});Q78=makeQuery(id+"F0.imprint","IMPRINT",FACE,{"disambiguationData":[TD([[makeQuery(id+"F0.imprint","IMPRINT",EDGE,{"disambiguationData":[TD([[subQ2,-1.0]])],"derivedFrom":subQ1}),1.0]])]});}
            var Q79;
            {var subQ0=sQuery(id+"F0.wireOp",EDGE,"E3.14.0.0");var subQ1=sQuery(id+"F0.wireOp",EDGE,"a2V2KlfY-Gady-qtY6-GD2h-aRWodLEw3NTq.top");var subQ2=makeQuery(id+"F0.imprint","INTERSECT",VERTEX,{"derivedFrom":[subQ1,subQ0]});Q79=makeQuery(id+"F0.imprint","IMPRINT",FACE,{"disambiguationData":[TD([[makeQuery(id+"F0.imprint","IMPRINT",EDGE,{"disambiguationData":[TD([[subQ2,-1.0]])],"derivedFrom":subQ1}),1.0]])]});}
            var Q80;
            Q80=makeQuery(id+"F0.imprint","IMPRINT",FACE,{"disambiguationData":[TD([[makeQuery(id+"F0.imprint","IMPRINT",EDGE,{"derivedFrom":sQuery(id+"F0.wireOp",EDGE,"E5.0.16.0")}),1.0]])]});
            var Q81;
            Q81=makeQuery(id+"F0.imprint","IMPRINT",FACE,{"disambiguationData":[TD([[makeQuery(id+"F0.imprint","IMPRINT",EDGE,{"derivedFrom":sQuery(id+"F0.wireOp",EDGE,"E5.0.17.0")}),1.0]])]});
            var Q82;
            Q82=makeQuery(id+"F0.imprint","IMPRINT",FACE,{"disambiguationData":[TD([[makeQuery(id+"F0.imprint","IMPRINT",EDGE,{"derivedFrom":sQuery(id+"F0.wireOp",EDGE,"E5.0.18.0")}),1.0]])]});
            var Q83;
            Q83=makeQuery(id+"F0.imprint","IMPRINT",FACE,{"disambiguationData":[TD([[makeQuery(id+"F0.imprint","IMPRINT",EDGE,{"derivedFrom":sQuery(id+"F0.wireOp",EDGE,"E5.0.19.0")}),1.0]])]});
            var Q84;
            Q84=makeQuery(id+"F0.imprint","IMPRINT",FACE,{"disambiguationData":[TD([[makeQuery(id+"F0.imprint","IMPRINT",EDGE,{"derivedFrom":sQuery(id+"F0.wireOp",EDGE,"E5.0.20.0")}),1.0]])]});
            var Q85;
            Q85=makeQuery(id+"F0.imprint","IMPRINT",FACE,{"disambiguationData":[TD([[makeQuery(id+"F0.imprint","IMPRINT",EDGE,{"derivedFrom":sQuery(id+"F0.wireOp",EDGE,"E5.0.21.0")}),1.0]])]});
            var Q86;
            Q86=makeQuery(id+"F0.imprint","IMPRINT",FACE,{"disambiguationData":[TD([[makeQuery(id+"F0.imprint","IMPRINT",EDGE,{"derivedFrom":sQuery(id+"F0.wireOp",EDGE,"E5.0.22.0")}),1.0]])]});
            var Q87;
            Q87=makeQuery(id+"F0.imprint","IMPRINT",FACE,{"disambiguationData":[TD([[makeQuery(id+"F0.imprint","IMPRINT",EDGE,{"derivedFrom":sQuery(id+"F0.wireOp",EDGE,"E6.0.23.0")}),1.0]])]});
            var Q88;
            Q88=makeQuery(id+"F0.imprint","IMPRINT",FACE,{"disambiguationData":[TD([[makeQuery(id+"F0.imprint","IMPRINT",EDGE,{"derivedFrom":sQuery(id+"F0.wireOp",EDGE,"E6.0.24.0")}),1.0]])]});
            var Q89;
            Q89=makeQuery(id+"F0.imprint","IMPRINT",FACE,{"disambiguationData":[TD([[makeQuery(id+"F0.imprint","IMPRINT",EDGE,{"derivedFrom":sQuery(id+"F0.wireOp",EDGE,"E6.0.25.0")}),1.0]])]});
            var Q90;
            Q90=makeQuery(id+"F0.imprint","IMPRINT",FACE,{"disambiguationData":[TD([[makeQuery(id+"F0.imprint","IMPRINT",EDGE,{"derivedFrom":sQuery(id+"F0.wireOp",EDGE,"E6.0.26.0")}),1.0]])]});
            var Q91;
            Q91=makeQuery(id+"F0.imprint","IMPRINT",FACE,{"disambiguationData":[TD([[makeQuery(id+"F0.imprint","IMPRINT",EDGE,{"derivedFrom":sQuery(id+"F0.wireOp",EDGE,"E6.0.27.0")}),1.0]])]});
            var Q92;
            Q92=makeQuery(id+"F0.imprint","IMPRINT",FACE,{"disambiguationData":[TD([[makeQuery(id+"F0.imprint","IMPRINT",EDGE,{"derivedFrom":sQuery(id+"F0.wireOp",EDGE,"E7.0.28.0")}),1.0]])]});
            extrude(context, id + "F1", {"entities" : qUnion([Q0, Q1, Q2, Q3, Q4, Q5, Q6, Q7, Q8, Q9, Q10, Q11, Q12, Q13, Q14, Q15, Q16, Q17, Q18, Q19, Q20, Q21, Q22, Q23, Q24, Q25, Q26, Q27, Q28, Q29, Q30, Q31, Q32, Q33, Q34, Q35, Q36, Q37, Q38, Q39, Q40, Q41, Q42, Q43, Q44, Q45, Q46, Q47, Q48, Q49, Q50, Q51, Q52, Q53, Q54, Q55, Q56, Q57, Q58, Q59, Q60, Q61, Q62, Q63, Q64, Q65, Q66, Q67, Q68, Q69, Q70, Q71, Q72, Q73, Q74, Q75, Q76, Q77, Q78, Q79, Q80, Q81, Q82, Q83, Q84, Q85, Q86, Q87, Q88, Q89, Q90, Q91, Q92]), "depth" : 50 * mm});
        }
        {
            var Q0;
            Q0=qCreatedBy(makeId("Top.planeOp"),FACE);
            var sketch = newSketch(context, id + "F2", { "sketchPlane" : qUnion([Q0])});
            skLineSegment(sketch, "E8.bottom", {"start": v(0, 0) * mm, "end": v(3570, 0) * mm, "construction": true});
            skLineSegment(sketch, "E8.top", {"start": v(0, 1500) * mm, "end": v(3570, 1500) * mm, "construction": true});
            skLineSegment(sketch, "E8.left", {"start": v(0, 0) * mm, "end": v(0, 1500) * mm, "construction": true});
            skLineSegment(sketch, "E8.right", {"start": v(3570, 0) * mm, "end": v(3570, 1500) * mm, "construction": true});
            skLineSegment(sketch, "E9", {"start": v(0, 750) * mm, "end": v(3570, 750) * mm, "construction": true});
            skLineSegment(sketch, "E10.bottom", {"start": v(0, 200) * mm, "end": v(3570, 200) * mm});
            skLineSegment(sketch, "E10.top", {"start": v(0, 150) * mm, "end": v(3570, 150) * mm});
            skLineSegment(sketch, "E10.left", {"start": v(0, 200) * mm, "end": v(0, 150) * mm});
            skLineSegment(sketch, "E10.right", {"start": v(3570, 200) * mm, "end": v(3570, 150) * mm});
            skLineSegment(sketch, "E11.MirrorCS", {"start": v(0, 1300) * mm, "end": v(0, 1350) * mm});
            skLineSegment(sketch, "E12.MirrorCS", {"start": v(3570, 1300) * mm, "end": v(3570, 1350) * mm});
            skLineSegment(sketch, "E13.MirrorCS", {"start": v(0, 1300) * mm, "end": v(3570, 1300) * mm});
            skLineSegment(sketch, "E14.MirrorCS", {"start": v(0, 1350) * mm, "end": v(3570, 1350) * mm});
            skSolve(sketch);
        }
        {
            var Q0;
            Q0=qSketchRegion(id+"F2",true);
            extrude(context, id + "F3", {"entities" : qUnion([Q0]), "oppositeDirection" : true, "depth" : 25 * mm});
        }
    });
